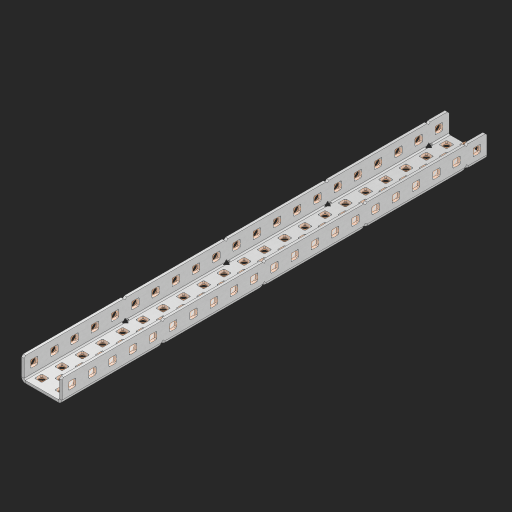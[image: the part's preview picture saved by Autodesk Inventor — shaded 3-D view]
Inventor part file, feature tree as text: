
AUTODESK INVENTOR PART (.ipt)
format: ipt  version: 2023 (Build 270158000, 158)  size: 1,464,320 bytes
history: native  units: in
note: dims shown in document units (in); Inventor stores cm internally (conversion verified against a paired STEP export)
features: other x112, extrude x103, sheet_metal_op x11, sketch x10, pattern_linear x2, mirror x1, chamfer x1
ambient origin geometry x8: Origin, YZ Plane, XZ Plane, XY Plane, X Axis, Y Axis, Z Axis, Center Point
bodies: Solid1 (feature_tree), Body (feature_tree)
feature tree (240):
  sheet_metal_op  "Flanges"
  other  "Flange Pattern Plane"
  other  "Flange Pattern Sketch"
  sheet_metal_op  "Flange Pattern"
  sheet_metal_op  "Body Pattern"
  pattern_linear  "Center Pattern"  Spacing1=0.0625in  [1 undecoded]
  other  "Arc Length"
  mirror  "Notch Mirror"
  pattern_linear  "Notch Pattern"  Spacing1=0.182in  [1 undecoded]
  chamfer  "End Chamfer"
  extrude  "Half Cut"  Depth=0.02in
  sketch  "Sketch1"  dims[d0=1.0in]
  other  "Plate1"
  sketch  "Sketch2"  dims[d1=10.5in]
  other  "Plate2"
  sheet_metal_op  "Bend1"
  sheet_metal_op  "Corner1"
  sketch  "Sketch3"  dims[d2=0.0625in]
  sketch  "Sketch7"  dims[d3=0.0625in]
  other  "Srf1"
  other  "Srf2"
  sketch  "Sketch8"  dims[d4=0.0312in]
  sketch  "Sketch9"  dims[d5=0.125in]
  other  "Srf91"
  sheet_metal_op  "Body Pattern Sketch"
  other  "Srf92"
  sketch  "Sketch13"  dims[d6=0.0625in]
  sketch  "Sketch14"  dims[d7=0.5in d8=90.0deg d9=0.0312in]
  sketch  "Sketch15"  dims[d10=0.25in]
  sketch  "Sketch16"  dims[d11=0.0625in d12=0.0625in d16=0.182in d17=0.02in d18=0.0625in d19=0.0in d20=0.25in d21=0.25in d38=8.2677in d40=0.5in d41=0.7874in d43=1.0in d46=0.172in d47=1.0in d48=0.0in d49=0.182in d50=0.02in d51=0.25in d52=0.25in d53=0.0625in d54=0.0in d55=0.172in d56=1.0in d57=0.0in d58=0.25in d60=8.2677in d62=0.5in d63=0.7874in d65=0.5in d85=0.1473in d86=0.1782in d88=0.04in d89=0.0625in d90=0.0in d91=0.04in d92=0.0491in d95=2.5in d96=0.04in d97=0.25in d98=45.0deg d99=0.25in d100=0.5in d101=0.0in d102=2.497in d106=0.182in d107=0.02in d108=0.5in d109=0.5in d110=0.0625in d111=0.0in d112=0.172in d113=0.5in d114=0.0in d117=0.5in d118=0.5in d119=0.5in]
  other  "Srf786"
  other  "Srf823"
  other  "Srf824"
  other  "Srf825"
  other  "Srf826"
  other  "Srf827"
  other  "Srf828"
  other  "Srf829"
  other  "Srf856"
  other  "Srf857"
  other  "Srf858"
  other  "Srf859"
  other  "Srf860"
  other  "Srf861"
  other  "Srf862"
  other  "Srf889"
  other  "Srf890"
  other  "Srf891"
  other  "Srf892"
  other  "Srf893"
  other  "Srf894"
  other  "Srf895"
  other  "Srf896"
  other  "Srf922"
  other  "Srf923"
  other  "Srf924"
  other  "Srf925"
  other  "Srf926"
  other  "Srf959"
  other  "Srf960"
  other  "Srf961"
  other  "Srf962"
  other  "Srf963"
  other  "Srf996"
  other  "Srf997"
  other  "Srf998"
  other  "Srf999"
  other  "Srf1000"
  other  "Srf1143"
  other  "Srf1144"
  other  "Srf1145"
  other  "Srf1146"
  other  "Srf1147"
  other  "Srf1148"
  other  "Srf1149"
  other  "Srf1150"
  other  "Srf1151"
  other  "Srf1152"
  other  "Srf1153"
  other  "Srf1154"
  other  "Srf1155"
  other  "Srf1156"
  other  "Srf1157"
  other  "Srf1158"
  other  "Srf1159"
  other  "Srf1160"
  other  "Srf1161"
  other  "Srf1162"
  other  "Srf1163"
  other  "Srf1164"
  other  "Srf1165"
  other  "Srf1166"
  other  "Srf1167"
  other  "Srf1168"
  other  "Srf1169"
  other  "Srf1170"
  other  "Srf1199"
  other  "Srf1200"
  other  "Srf1201"
  other  "Srf1202"
  other  "Srf1203"
  other  "Srf1204"
  other  "Srf1205"
  other  "Srf1206"
  other  "Srf1207"
  other  "Srf1208"
  other  "Srf1209"
  other  "Srf1210"
  other  "Srf1211"
  other  "Srf1212"
  other  "Srf1213"
  other  "Srf1214"
  other  "Srf1215"
  other  "Srf1216"
  other  "Srf1217"
  other  "Srf1218"
  other  "Srf1219"
  other  "Srf1220"
  other  "Srf1221"
  other  "Srf1222"
  other  "Srf1223"
  other  "Srf1224"
  other  "Srf1225"
  other  "Srf1226"
  other  "Srf1255"
  other  "Srf1256"
  other  "Srf1257"
  other  "Srf1258"
  other  "Srf1259"
  other  "Srf1260"
  other  "Srf1261"
  sheet_metal_op  "Flange Stamp"
  sheet_metal_op  "Flange Circle"
  sheet_metal_op  "Body Stamp"
  sheet_metal_op  "Body Circle"
  other  "Center Stamp"
  other  "Center Circle"
  sheet_metal_op  "Notch"
  extrude  "ExtrusionSrf2"  Depth=0.0625in
  extrude  "ExtrusionSrf92"  TaperAngle=0.0deg  [1 undecoded]
  extrude  "ExtrusionSrf823"  Depth=0.5in
  extrude  "ExtrusionSrf824"  Depth=0.5in
  extrude  "ExtrusionSrf825"  Depth=0.5in
  extrude  "ExtrusionSrf826"  Depth=0.5in
  extrude  "ExtrusionSrf827"  Depth=1.0in TaperAngle=0.0deg
  extrude  "ExtrusionSrf828"  Depth=0.5in
  extrude  "ExtrusionSrf829"  Depth=0.02in
  extrude  "ExtrusionSrf856"  Depth=0.5in
  extrude  "ExtrusionSrf857"  Depth=0.5in
  extrude  "ExtrusionSrf858"  Depth=0.0625in
  extrude  "ExtrusionSrf859"  TaperAngle=0.0deg  [1 undecoded]
  extrude  "ExtrusionSrf860"  Depth=0.5in
  extrude  "ExtrusionSrf861"  Depth=1.0in TaperAngle=0.0deg
  extrude  "ExtrusionSrf862"  Depth=0.5in
  extrude  "ExtrusionSrf889"  Depth=0.5in
  extrude  "ExtrusionSrf890"  Depth=0.5in
  extrude  "ExtrusionSrf891"  Depth=0.5in
  extrude  "ExtrusionSrf892"  Depth=0.5in
  extrude  "ExtrusionSrf893"  Depth=0.5in
  extrude  "ExtrusionSrf894"  Depth=0.0625in
  extrude  "ExtrusionSrf895"  TaperAngle=0.0deg  [1 undecoded]
  extrude  "ExtrusionSrf896"  Depth=0.5in
  extrude  "ExtrusionSrf922"  Depth=0.5in
  extrude  "ExtrusionSrf923"  Depth=2.5in
  extrude  "ExtrusionSrf924"  Depth=0.5in TaperAngle=45.0deg
  extrude  "ExtrusionSrf925"  Depth=0.5in
  extrude  "ExtrusionSrf926"  Depth=0.5in TaperAngle=0.0deg
  extrude  "ExtrusionSrf959"  Depth=0.5in
  extrude  "ExtrusionSrf960"  Depth=0.5in
  extrude  "ExtrusionSrf961"  Depth=0.02in
  extrude  "ExtrusionSrf962"  Depth=0.5in
  extrude  "ExtrusionSrf963"  Depth=0.5in
  extrude  "ExtrusionSrf996"  Depth=0.0625in
  extrude  "ExtrusionSrf997"  TaperAngle=0.0deg  [1 undecoded]
  extrude  "ExtrusionSrf998"  Depth=0.5in
  extrude  "ExtrusionSrf999"  Depth=0.5in TaperAngle=0.0deg
  extrude  "ExtrusionSrf1000"  Depth=0.5in
  extrude  "ExtrusionSrf1143"  Depth=0.5in
  extrude  "ExtrusionSrf1144"  Depth=0.5in
  extrude  "ExtrusionSrf1145"  [1 undecoded]
  extrude  "ExtrusionSrf1146"  [1 undecoded]
  extrude  "ExtrusionSrf1147"  [1 undecoded]
  extrude  "ExtrusionSrf1148"  [1 undecoded]
  extrude  "ExtrusionSrf1149"  [1 undecoded]
  extrude  "ExtrusionSrf1150"  [1 undecoded]
  extrude  "ExtrusionSrf1151"  [1 undecoded]
  extrude  "ExtrusionSrf1152"  [1 undecoded]
  extrude  "ExtrusionSrf1153"  [1 undecoded]
  extrude  "ExtrusionSrf1154"  [1 undecoded]
  extrude  "ExtrusionSrf1155"  [1 undecoded]
  extrude  "ExtrusionSrf1156"  [1 undecoded]
  extrude  "ExtrusionSrf1157"  [1 undecoded]
  extrude  "ExtrusionSrf1158"  [1 undecoded]
  extrude  "ExtrusionSrf1159"  [1 undecoded]
  extrude  "ExtrusionSrf1160"  [1 undecoded]
  extrude  "ExtrusionSrf1161"  [1 undecoded]
  extrude  "ExtrusionSrf1162"  [1 undecoded]
  extrude  "ExtrusionSrf1163"  [1 undecoded]
  extrude  "ExtrusionSrf1164"  [1 undecoded]
  extrude  "ExtrusionSrf1165"  [1 undecoded]
  extrude  "ExtrusionSrf1166"  [1 undecoded]
  extrude  "ExtrusionSrf1167"  [1 undecoded]
  extrude  "ExtrusionSrf1168"  [1 undecoded]
  extrude  "ExtrusionSrf1169"  [1 undecoded]
  extrude  "ExtrusionSrf1170"  [1 undecoded]
  extrude  "ExtrusionSrf1199"  [1 undecoded]
  extrude  "ExtrusionSrf1200"  [1 undecoded]
  extrude  "ExtrusionSrf1201"  [1 undecoded]
  extrude  "ExtrusionSrf1202"  [1 undecoded]
  extrude  "ExtrusionSrf1203"  [1 undecoded]
  extrude  "ExtrusionSrf1204"  [1 undecoded]
  extrude  "ExtrusionSrf1205"  [1 undecoded]
  extrude  "ExtrusionSrf1206"  [1 undecoded]
  extrude  "ExtrusionSrf1207"  [1 undecoded]
  extrude  "ExtrusionSrf1208"  [1 undecoded]
  extrude  "ExtrusionSrf1209"  [1 undecoded]
  extrude  "ExtrusionSrf1210"  [1 undecoded]
  extrude  "ExtrusionSrf1211"  [1 undecoded]
  extrude  "ExtrusionSrf1212"  [1 undecoded]
  extrude  "ExtrusionSrf1213"  [1 undecoded]
  extrude  "ExtrusionSrf1214"  [1 undecoded]
  extrude  "ExtrusionSrf1215"  [1 undecoded]
  extrude  "ExtrusionSrf1216"  [1 undecoded]
  extrude  "ExtrusionSrf1217"  [1 undecoded]
  extrude  "ExtrusionSrf1218"  [1 undecoded]
  extrude  "ExtrusionSrf1219"  [1 undecoded]
  extrude  "ExtrusionSrf1220"  [1 undecoded]
  extrude  "ExtrusionSrf1221"  [1 undecoded]
  extrude  "ExtrusionSrf1222"  [1 undecoded]
  extrude  "ExtrusionSrf1223"  [1 undecoded]
  extrude  "ExtrusionSrf1224"  [1 undecoded]
  extrude  "ExtrusionSrf1225"  [1 undecoded]
  extrude  "ExtrusionSrf1226"  [1 undecoded]
  extrude  "ExtrusionSrf1255"  [1 undecoded]
  extrude  "ExtrusionSrf1256"  [1 undecoded]
  extrude  "ExtrusionSrf1257"  [1 undecoded]
  extrude  "ExtrusionSrf1258"  [1 undecoded]
  extrude  "ExtrusionSrf1259"  [1 undecoded]
  extrude  "ExtrusionSrf1260"  [1 undecoded]
  extrude  "ExtrusionSrf1261"  [1 undecoded]
note: 67 required parameter values undecoded (feature->parameter linkage not recoverable at this tier; creation-order binding heuristic only, values carry confidence <= 0.55)
